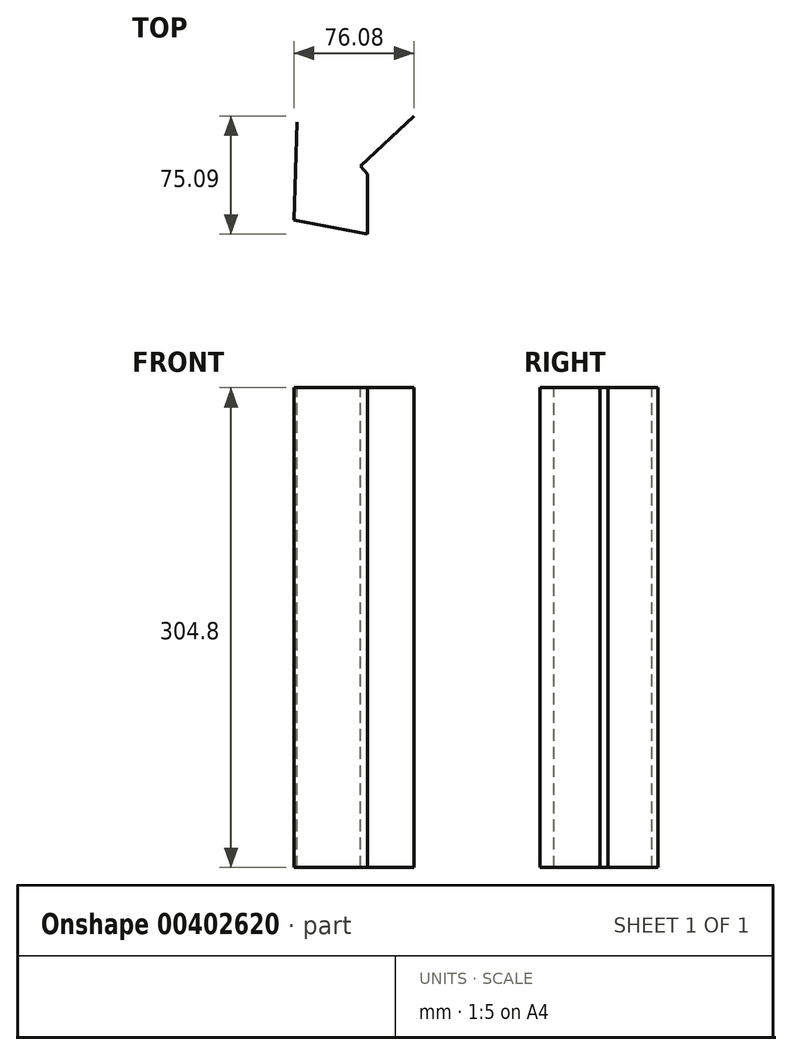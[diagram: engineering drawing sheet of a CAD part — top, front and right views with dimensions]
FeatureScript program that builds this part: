
annotation { "Feature Type Name" : "Feature", "Feature Type Description" : "" }
export const myFeature = defineFeature(function(context is Context, id is Id, definition is map)
    precondition{}
    {
        {
            var Q0;
            Q0=qCreatedBy(makeId("Top.planeOp"),FACE);
            var sketch = newSketch(context, id + "F0", { "sketchPlane" : qUnion([Q0])});
            skLineSegment(sketch, "E0", {"start": v(0, 0) * mm, "end": v(0, -38.04) * mm});
            skLineSegment(sketch, "E1", {"start": v(0, -38.04) * mm, "end": v(-46.73, -29.18) * mm});
            skLineSegment(sketch, "E2", {"start": v(-46.73, -29.18) * mm, "end": v(-44.76, 33.28) * mm});
            skLineSegment(sketch, "E3", {"start": v(-44.76, 33.28) * mm, "end": v(29.35, 37.05) * mm});
            skLineSegment(sketch, "E4", {"start": v(29.35, 37.05) * mm, "end": v(-4.43, 5.25) * mm});
            skLineSegment(sketch, "E5", {"start": v(-4.43, 5.25) * mm, "end": v(0, 0) * mm});
            skSolve(sketch);
        }
        {
            var Q0;
            Q0 = qSketchRegion(id + "F0", true);
            var Q1;
            Q1=sQuery(id+"F0.wireOp",EDGE,"E2");
            var Q2;
            Q2=sQuery(id+"F0.wireOp",EDGE,"E1");
            var Q3;
            Q3=sQuery(id+"F0.wireOp",EDGE,"E0");
            var Q4;
            Q4=sQuery(id+"F0.wireOp",EDGE,"E5");
            var Q5;
            Q5=sQuery(id+"F0.wireOp",EDGE,"E4");
            extrude(context, id + "F1", {"entities" : qUnion([Q0]), "bodyType" : ToolBodyType.SURFACE, "operationType" : NewBodyOperationType.ADD, "surfaceEntities" : qUnion([Q1, Q2, Q3, Q4, Q5]), "depth" : 304.8 * mm});
        }
    });
